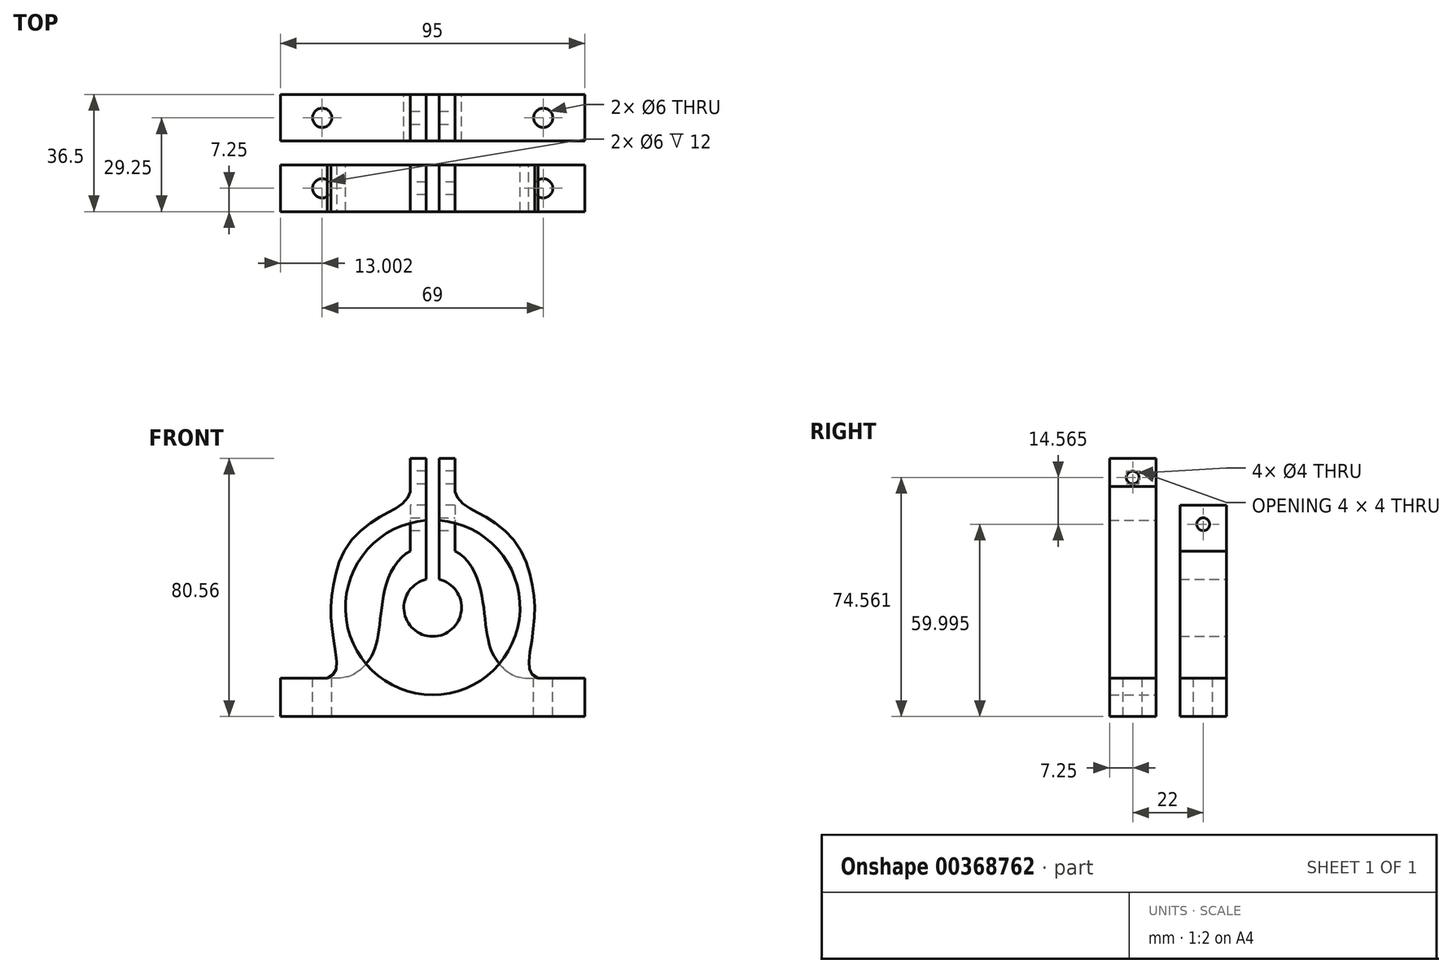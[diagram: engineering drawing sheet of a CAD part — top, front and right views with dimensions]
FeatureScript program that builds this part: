
annotation { "Feature Type Name" : "Feature", "Feature Type Description" : "" }
export const myFeature = defineFeature(function(context is Context, id is Id, definition is map)
    precondition{}
    {
        {
            var Q0;
            Q0=qCreatedBy(makeId("Front.planeOp"),FACE);
            var sketch = newSketch(context, id + "F0", { "sketchPlane" : qUnion([Q0])});
            skLineSegment(sketch, "E0", {"start": v(0, 70) * mm, "end": v(-7, 70) * mm});
            skLineSegment(sketch, "E1", {"start": v(-7, 70) * mm, "end": v(-7, 55.6) * mm});
            skFitSpline(sketch, "E2", {"points": [v(-7, 55.6) * mm, v(-12.84, 49.4) * mm, v(-15.58, 40.31) * mm, v(-16.44, 30.88) * mm, v(-18.28, 24.56) * mm, v(-20, 21.13) * mm, v(-23.28, 17.3) * mm, v(-29.5, 16) * mm], "startDerivative": vector(-41.03, -17.29) * mm, "endDerivative": vector(-26.14, 0) * mm});
            skLineSegment(sketch, "E3", {"start": v(-29.5, 16) * mm, "end": v(-47.5, 16) * mm});
            skLineSegment(sketch, "E4", {"start": v(-47.5, 16) * mm, "end": v(-47.5, 4) * mm});
            skLineSegment(sketch, "E5", {"start": v(-47.5, 4) * mm, "end": v(0, 4) * mm});
            skLineSegment(sketch, "E6", {"start": v(0, 4) * mm, "end": v(0, 29) * mm});
            skArc(sketch, "E7", {"start": v(0, 47) * mm, "mid": v(-9, 38) * mm, "end": v(0, 29) * mm});
            skLineSegment(sketch, "E8", {"start": v(0, 47) * mm, "end": v(0, 70) * mm});
            skPoint(sketch, "E9", {"position": v(-34.5, 16) * mm});
            skSolve(sketch);
        }
        {
            var Q0;
            Q0=makeQuery(id+"F0.imprint","IMPRINT",FACE,{"disambiguationData":[TD([[makeQuery(id+"F0.imprint","IMPRINT",EDGE,{"derivedFrom":sQuery(id+"F0.wireOp",EDGE,"E0")}),1.0]])]});
            var sketch = newSketch(context, id + "F1", { "sketchPlane" : qUnion([Q0])});
            skLineSegment(sketch, "E10", {"start": v(-202.57, 88.33) * mm, "end": v(-209.57, 88.33) * mm});
            skLineSegment(sketch, "E11", {"start": v(-209.57, 88.33) * mm, "end": v(-209.57, 73.93) * mm});
            skFitSpline(sketch, "E12", {"points": [v(-209.57, 73.93) * mm, v(-215.4, 67.73) * mm, v(-218.15, 58.64) * mm, v(-219.2, 50.4) * mm, v(-220.4, 44.2) * mm, v(-222.37, 40.06) * mm, v(-227.38, 35.38) * mm, v(-232.07, 34.33) * mm], "startDerivative": vector(-41.03, -17.29) * mm, "endDerivative": vector(-26.14, 0) * mm});
            skLineSegment(sketch, "E13", {"start": v(-232.07, 34.33) * mm, "end": v(-250.07, 34.33) * mm});
            skLineSegment(sketch, "E14", {"start": v(-250.07, 34.33) * mm, "end": v(-250.07, 22.33) * mm});
            skLineSegment(sketch, "E15", {"start": v(-250.07, 22.33) * mm, "end": v(-202.57, 22.33) * mm});
            skLineSegment(sketch, "E16", {"start": v(-202.57, 22.33) * mm, "end": v(-202.57, 47.33) * mm});
            skArc(sketch, "E17", {"start": v(-202.57, 65.33) * mm, "mid": v(-211.57, 56.33) * mm, "end": v(-202.57, 47.33) * mm});
            skLineSegment(sketch, "E18", {"start": v(-202.57, 65.33) * mm, "end": v(-202.57, 88.33) * mm});
            skLineSegment(sketch, "E19", {"start": v(-202.57, 112.52) * mm, "end": v(-202.57, -11.67) * mm, "construction": true});
            skLineSegment(sketch, "E20.MirrorCS", {"start": v(-155.07, 22.33) * mm, "end": v(-202.57, 22.33) * mm});
            skLineSegment(sketch, "E21.MirrorCS", {"start": v(-202.57, 88.33) * mm, "end": v(-195.57, 88.33) * mm});
            skFitSpline(sketch, "E22.MirrorCS", {"points": [v(-195.57, 73.93) * mm, v(-189.73, 67.73) * mm, v(-186.98, 58.64) * mm, v(-185.93, 50.4) * mm, v(-184.73, 44.2) * mm, v(-182.77, 40.06) * mm, v(-177.76, 35.38) * mm, v(-173.07, 34.33) * mm], "startDerivative": vector(41.03, -17.29) * mm, "endDerivative": vector(26.14, 0) * mm});
            skLineSegment(sketch, "E23.MirrorCS", {"start": v(-155.07, 34.33) * mm, "end": v(-155.07, 22.33) * mm});
            skLineSegment(sketch, "E24.MirrorCS", {"start": v(-195.57, 88.33) * mm, "end": v(-195.57, 73.93) * mm});
            skLineSegment(sketch, "E25.MirrorCS", {"start": v(-173.07, 34.33) * mm, "end": v(-155.07, 34.33) * mm});
            skArc(sketch, "E26.MirrorCS", {"start": v(-202.57, 65.33) * mm, "mid": v(-193.57, 56.33) * mm, "end": v(-202.57, 47.33) * mm});
            skSolve(sketch);
        }
        {
            var Q0;
            Q0 = qSketchRegion(id + "F1", true);
            extrude(context, id + "F2", {"entities" : qUnion([Q0]), "depth" : 14.5 * mm, "offsetDistance" : 25 * mm});
        }
        {
            var Q0;
            Q0=makeQuery(id+"F2.opExtrude","SWEPT_FACE",FACE,{"disambiguationData":[OSD([sQuery(id+"F1.wireOp",EDGE,"E13")])]});
            var sketch = newSketch(context, id + "F3", { "sketchPlane" : qUnion([Q0])});
            skCircle(sketch, "E27", {"center": v(-237.07, -7.25) * mm, "radius": 3 * mm});
            skPoint(sketch, "E27.centerSnap0", {"position": v(-250.07, -7.25) * mm});
            skCircle(sketch, "E28", {"center": v(-168.07, -7.25) * mm, "radius": 3 * mm});
            skPoint(sketch, "E29", {"position": v(-241.07, -14.5) * mm});
            skSolve(sketch);
        }
        {
            var Q0;
            Q0=makeQuery(id+"F3.imprint","IMPRINT",FACE,{"disambiguationData":[TD([[makeQuery(id+"F3.imprint","IMPRINT",EDGE,{"derivedFrom":sQuery(id+"F3.wireOp",EDGE,"E27")}),1.0]])]});
            var Q1;
            Q1=makeQuery(id+"F3.imprint","IMPRINT",FACE,{"disambiguationData":[TD([[makeQuery(id+"F3.imprint","IMPRINT",EDGE,{"derivedFrom":sQuery(id+"F3.wireOp",EDGE,"E28")}),1.0]])]});
            extrude(context, id + "F4", {"entities" : qUnion([Q0, Q1]), "operationType" : NewBodyOperationType.REMOVE, "oppositeDirection" : true, "depth" : 25 * mm, "offsetDistance" : 25 * mm});
        }
        {
            var Q0;
            Q0=makeQuery(id+"F2.opExtrude","SWEPT_FACE",FACE,{"disambiguationData":[OSD([sQuery(id+"F1.wireOp",EDGE,"E10"),sQuery(id+"F1.wireOp",EDGE,"E21.MirrorCS")])]});
            var sketch = newSketch(context, id + "F5", { "sketchPlane" : qUnion([Q0])});
            skLineSegment(sketch, "E30.bottom", {"start": v(-200.57, -14.5) * mm, "end": v(-204.57, -14.5) * mm});
            skLineSegment(sketch, "E30.top", {"start": v(-200.57, 0) * mm, "end": v(-204.57, 0) * mm});
            skLineSegment(sketch, "E30.left", {"start": v(-200.57, -14.5) * mm, "end": v(-200.57, 0) * mm});
            skLineSegment(sketch, "E30.right", {"start": v(-204.57, -14.5) * mm, "end": v(-204.57, 0) * mm});
            skPoint(sketch, "E30.middle", {"position": v(-202.57, -7.25) * mm});
            skPoint(sketch, "E30.middle.positionSnap0", {"position": v(-202.57, 0) * mm});
            skPoint(sketch, "E30.centerSnap0", {"position": v(-202.57, 0) * mm});
            skSolve(sketch);
        }
        {
            var Q0;
            Q0 = qSketchRegion(id + "F5", true);
            extrude(context, id + "F6", {"entities" : qUnion([Q0]), "operationType" : NewBodyOperationType.REMOVE, "oppositeDirection" : true, "depth" : 25 * mm, "offsetDistance" : 25 * mm});
        }
        {
            var Q0;
            Q0=makeQuery(id+"F2.opExtrude","SWEPT_FACE",FACE,{"disambiguationData":[OSD([sQuery(id+"F1.wireOp",EDGE,"E24.MirrorCS")])]});
            var sketch = newSketch(context, id + "F7", { "sketchPlane" : qUnion([Q0])});
            skCircle(sketch, "E31", {"center": v(-7.25, 82.33) * mm, "radius": 2 * mm});
            skPoint(sketch, "E31.centerSnap0", {"position": v(-7.25, 88.33) * mm});
            skSolve(sketch);
        }
        {
            var Q0;
            Q0 = qSketchRegion(id + "F7", true);
            extrude(context, id + "F8", {"entities" : qUnion([Q0]), "operationType" : NewBodyOperationType.REMOVE, "oppositeDirection" : true, "depth" : 25 * mm, "offsetDistance" : 25 * mm});
        }
        {
            var Q0;
            Q0=qCreatedBy(makeId("Front.planeOp"),FACE);
            cPlane(context, id + "F9", {"entities" : qUnion([Q0]), "cplaneType" : CPlaneType.OFFSET, "offset" : 22 * mm, "width" : 150 * mm, "height" : 150 * mm});
        }
        {
            var Q0;
            Q0=qCreatedBy(id+"F9.planeOp",FACE);
            var sketch = newSketch(context, id + "F10", { "sketchPlane" : qUnion([Q0])});
            skCircle(sketch, "E32", {"center": v(-202.57, 56.33) * mm, "radius": 27.25 * mm});
            skFitSpline(sketch, "E33", {"points": [v(-235.48, 34.33) * mm, v(-232.88, 36.54) * mm, v(-233, 42.69) * mm, v(-234.36, 54.12) * mm, v(-233.5, 63.95) * mm, v(-228.95, 76) * mm, v(-219.36, 84.48) * mm, v(-213.33, 87.8) * mm, v(-209.77, 91.61) * mm, v(-209.57, 94.07) * mm], "startDerivative": vector(50.74, 19) * mm, "endDerivative": vector(1.63, 36.85) * mm});
            skLineSegment(sketch, "E34", {"start": v(-209.57, 94.07) * mm, "end": v(-209.57, 102.9) * mm});
            skLineSegment(sketch, "E35", {"start": v(-209.57, 102.9) * mm, "end": v(-204.57, 102.9) * mm});
            skLineSegment(sketch, "E36", {"start": v(-204.57, 102.9) * mm, "end": v(-204.57, 83.5) * mm});
            skLineSegment(sketch, "E37", {"start": v(-235.48, 34.33) * mm, "end": v(-250.07, 34.33) * mm});
            skLineSegment(sketch, "E38", {"start": v(-250.07, 34.33) * mm, "end": v(-250.07, 22.33) * mm});
            skLineSegment(sketch, "E39", {"start": v(-250.07, 22.33) * mm, "end": v(-202.63, 22.33) * mm});
            skLineSegment(sketch, "E40", {"start": v(-202.63, 22.33) * mm, "end": v(-202.63, 29.08) * mm});
            skLineSegment(sketch, "E41.MirrorCS", {"start": v(-195.57, 94.07) * mm, "end": v(-195.57, 102.9) * mm});
            skLineSegment(sketch, "E42.MirrorCS", {"start": v(-195.57, 102.9) * mm, "end": v(-200.57, 102.9) * mm});
            skLineSegment(sketch, "E43.MirrorCS", {"start": v(-200.57, 102.9) * mm, "end": v(-200.57, 83.5) * mm});
            skLineSegment(sketch, "E44.MirrorCS", {"start": v(-155.07, 22.33) * mm, "end": v(-202.5, 22.33) * mm});
            skLineSegment(sketch, "E45.MirrorCS", {"start": v(-155.07, 34.33) * mm, "end": v(-155.07, 22.33) * mm});
            skFitSpline(sketch, "E46.MirrorCS", {"points": [v(-169.65, 34.33) * mm, v(-172.26, 36.54) * mm, v(-172.13, 42.69) * mm, v(-170.78, 54.12) * mm, v(-171.64, 63.95) * mm, v(-176.19, 76) * mm, v(-185.78, 84.48) * mm, v(-191.8, 87.8) * mm, v(-195.37, 91.61) * mm, v(-195.57, 94.07) * mm], "startDerivative": vector(-50.74, 19) * mm, "endDerivative": vector(-1.63, 36.85) * mm});
            skLineSegment(sketch, "E47.MirrorCS", {"start": v(-169.65, 34.33) * mm, "end": v(-155.07, 34.33) * mm});
            skLineSegment(sketch, "E48", {"start": v(-250.07, 22.33) * mm, "end": v(-155.07, 22.33) * mm});
            skSolve(sketch);
        }
        {
            var Q0;
            Q0=makeQuery(id+"F10.imprint","IMPRINT",FACE,{"disambiguationData":[TD([[makeQuery(id+"F10.imprint","IMPRINT",EDGE,{"derivedFrom":sQuery(id+"F10.wireOp",EDGE,"E33")}),-1.0]])]});
            var Q1;
            {var subQ1=sQuery(id+"F10.wireOp",EDGE,"E40");Q1=makeQuery(id+"F10.imprint","IMPRINT",FACE,{"disambiguationData":[TD([[makeQuery(id+"F10.imprint","IMPRINT",EDGE,{"derivedFrom":subQ1}),-1.0]])]});}
            extrude(context, id + "F11", {"entities" : qUnion([Q0, Q1]), "depth" : 14.5 * mm, "offsetDistance" : 25 * mm});
        }
        {
            var Q0;
            Q0=makeQuery(id+"F11.opExtrude","SWEPT_FACE",FACE,{"disambiguationData":[OSD([sQuery(id+"F10.wireOp",EDGE,"E37")])]});
            var sketch = newSketch(context, id + "F12", { "sketchPlane" : qUnion([Q0])});
            skCircle(sketch, "E49", {"center": v(-237.07, -29.25) * mm, "radius": 3 * mm});
            skPoint(sketch, "E49.centerSnap0", {"position": v(-250.07, -29.25) * mm});
            skCircle(sketch, "E50", {"center": v(-168.07, -29.25) * mm, "radius": 3 * mm});
            skSolve(sketch);
        }
        {
            var Q0;
            Q0 = qSketchRegion(id + "F12", true);
            extrude(context, id + "F13", {"entities" : qUnion([Q0]), "operationType" : NewBodyOperationType.REMOVE, "oppositeDirection" : true, "depth" : 25 * mm, "offsetDistance" : 25 * mm});
        }
        {
            var Q0;
            Q0=makeQuery(id+"F11.opExtrude","SWEPT_FACE",FACE,{"disambiguationData":[OSD([sQuery(id+"F10.wireOp",EDGE,"E34")])]});
            var sketch = newSketch(context, id + "F14", { "sketchPlane" : qUnion([Q0])});
            skCircle(sketch, "E51", {"center": v(29.25, 96.9) * mm, "radius": 2 * mm});
            skPoint(sketch, "E51.centerSnap0", {"position": v(29.25, 102.9) * mm});
            skSolve(sketch);
        }
        {
            var Q0;
            Q0 = qSketchRegion(id + "F14", true);
            extrude(context, id + "F15", {"entities" : qUnion([Q0]), "operationType" : NewBodyOperationType.REMOVE, "oppositeDirection" : true, "depth" : 25 * mm, "offsetDistance" : 25 * mm});
        }
    });
